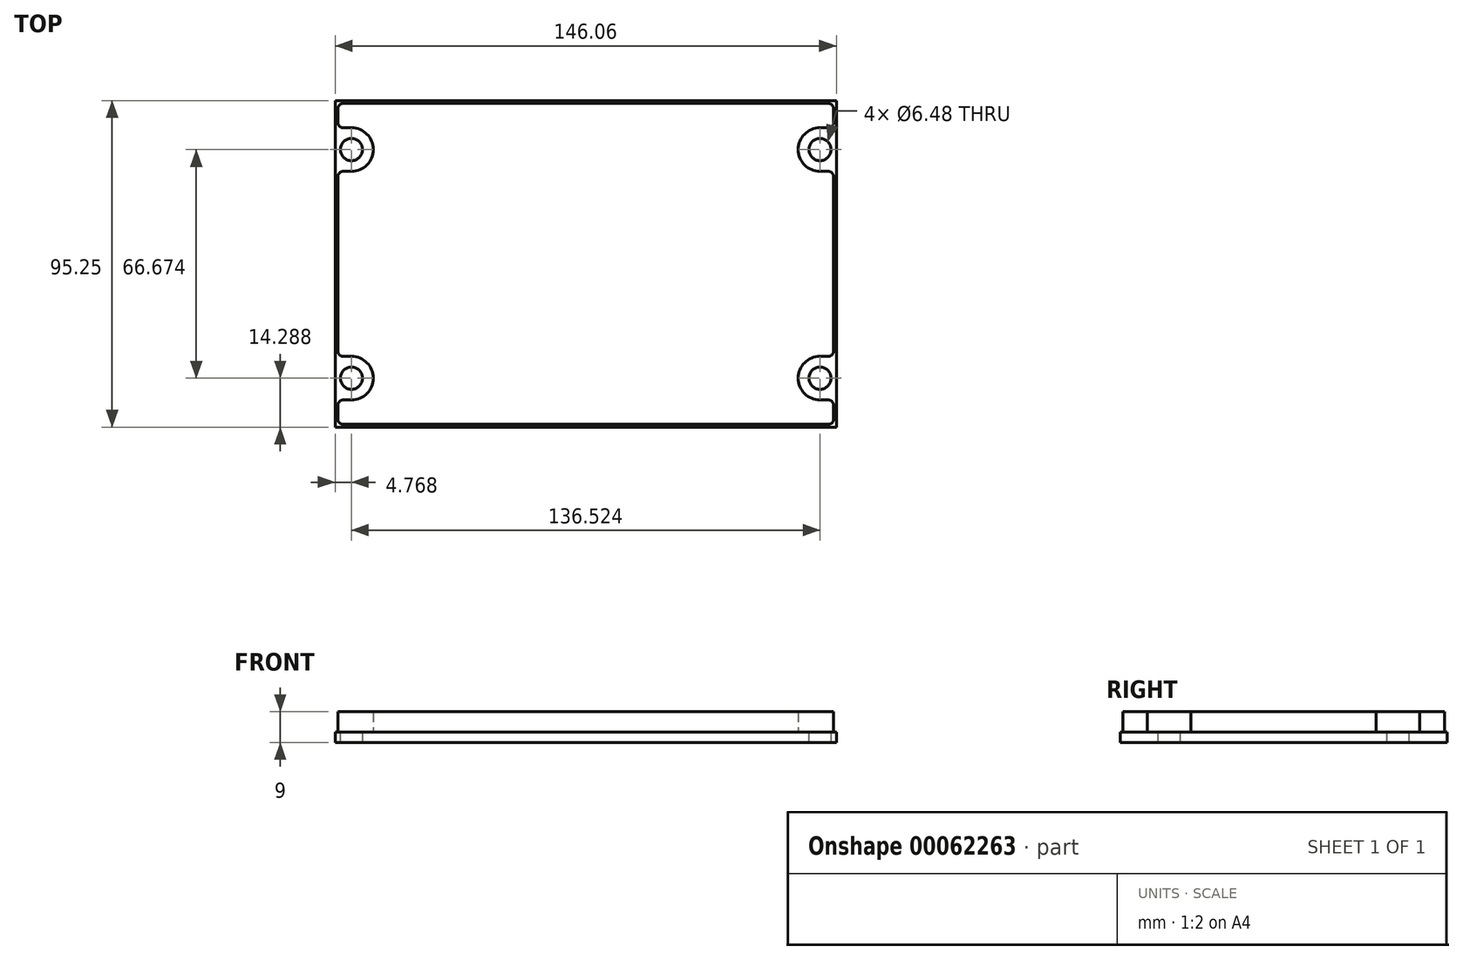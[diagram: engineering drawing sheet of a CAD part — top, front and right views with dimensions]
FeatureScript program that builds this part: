
annotation { "Feature Type Name" : "Feature", "Feature Type Description" : "" }
export const myFeature = defineFeature(function(context is Context, id is Id, definition is map)
    precondition{}
    {
        {
            var Q0;
            Q0=qCreatedBy(makeId("Top.planeOp"),FACE);
            var sketch = newSketch(context, id + "F0", { "sketchPlane" : qUnion([Q0])});
            skLineSegment(sketch, "E0.bottom", {"start": v(-73.03, 57.15) * mm, "end": v(73.03, 57.15) * mm});
            skLineSegment(sketch, "E0.top", {"start": v(-73.03, -38.1) * mm, "end": v(73.03, -38.1) * mm});
            skLineSegment(sketch, "E0.left", {"start": v(-73.03, 57.15) * mm, "end": v(-73.02, -38.1) * mm});
            skLineSegment(sketch, "E0.right", {"start": v(73.03, 57.15) * mm, "end": v(73.03, -38.1) * mm});
            skCircle(sketch, "E1", {"center": v(-68.26, 42.86) * mm, "radius": 3.24 * mm});
            skLineSegment(sketch, "E2", {"start": v(-73.03, 9.52) * mm, "end": v(-67.9, 9.52) * mm});
            skLineSegment(sketch, "E3.MirrorCS", {"start": v(73.03, 57.15) * mm, "end": v(73.02, -38.1) * mm});
            skCircle(sketch, "E4.MirrorC", {"center": v(68.26, 42.86) * mm, "radius": 3.24 * mm});
            skLineSegment(sketch, "E5.bottom", {"start": v(-72.23, 56.35) * mm, "end": v(72.23, 56.35) * mm});
            skLineSegment(sketch, "E5.top", {"start": v(-72.23, -37.3) * mm, "end": v(72.23, -37.3) * mm});
            skLineSegment(sketch, "E5.left", {"start": v(-72.22, 56.35) * mm, "end": v(-72.22, 49.21) * mm});
            skLineSegment(sketch, "E5.right", {"start": v(72.22, 56.35) * mm, "end": v(72.22, 49.21) * mm});
            skPoint(sketch, "E5.middle", {"position": v(0, 9.52) * mm});
            skPoint(sketch, "E5.middle.positionSnap0", {"position": v(0, 57.15) * mm});
            skPoint(sketch, "E5.centerSnap0", {"position": v(0, 57.15) * mm});
            skLineSegment(sketch, "E6.trimOffspring", {"start": v(-72.22, 36.51) * mm, "end": v(-72.22, -17.46) * mm});
            skCircle(sketch, "E7.MirrorC", {"center": v(-68.26, -23.81) * mm, "radius": 3.24 * mm});
            skLineSegment(sketch, "E8.trimOffspring", {"start": v(-72.22, -30.16) * mm, "end": v(-72.22, -37.3) * mm});
            skLineSegment(sketch, "E9", {"start": v(0, 59.28) * mm, "end": v(0, 57.15) * mm});
            skLineSegment(sketch, "E10.trimOffspring", {"start": v(72.22, 36.51) * mm, "end": v(72.22, -17.46) * mm});
            skLineSegment(sketch, "E11.trimOffspring", {"start": v(72.22, -30.16) * mm, "end": v(72.22, -37.3) * mm});
            skCircle(sketch, "E12.MirrorC", {"center": v(68.26, -23.81) * mm, "radius": 3.24 * mm});
            skLineSegment(sketch, "E13", {"start": v(-68.26, 49.21) * mm, "end": v(-72.22, 49.21) * mm});
            skLineSegment(sketch, "E14", {"start": v(-68.26, 36.51) * mm, "end": v(-72.22, 36.51) * mm});
            skArc(sketch, "E15.trimOffspring", {"start": v(-68.26, 36.51) * mm, "mid": v(-61.91, 42.86) * mm, "end": v(-68.26, 49.21) * mm});
            skLineSegment(sketch, "E16.MirrorCS", {"start": v(68.26, 49.21) * mm, "end": v(72.22, 49.21) * mm});
            skArc(sketch, "E17.MirrorCS", {"start": v(68.26, 36.51) * mm, "mid": v(61.91, 42.86) * mm, "end": v(68.26, 49.21) * mm});
            skLineSegment(sketch, "E18.MirrorCS", {"start": v(68.26, 36.51) * mm, "end": v(72.22, 36.51) * mm});
            skLineSegment(sketch, "E19.MirrorCS", {"start": v(-68.26, -30.16) * mm, "end": v(-72.22, -30.16) * mm});
            skArc(sketch, "E20.MirrorCS", {"start": v(-68.26, -17.46) * mm, "mid": v(-61.91, -23.81) * mm, "end": v(-68.26, -30.16) * mm});
            skLineSegment(sketch, "E21.MirrorCS", {"start": v(-68.26, -17.46) * mm, "end": v(-72.22, -17.46) * mm});
            skLineSegment(sketch, "E22.MirrorCS", {"start": v(68.26, -30.16) * mm, "end": v(72.23, -30.16) * mm});
            skArc(sketch, "E23.MirrorCS", {"start": v(68.26, -17.46) * mm, "mid": v(61.91, -23.81) * mm, "end": v(68.26, -30.16) * mm});
            skLineSegment(sketch, "E24.MirrorCS", {"start": v(68.26, -17.46) * mm, "end": v(72.23, -17.46) * mm});
            skSolve(sketch);
        }
        {
            var Q0;
            {var subQ3=sQuery(id+"F0.wireOp",EDGE,"E0.bottom");Q0=makeQuery(id+"F0.imprint","IMPRINT",FACE,{"disambiguationData":[TD([[makeQuery(id+"F0.imprint","IMPRINT",EDGE,{"derivedFrom":subQ3}),-1.0]])]});}
            var Q1;
            Q1=makeQuery(id+"F0.imprint","IMPRINT",FACE,{"disambiguationData":[TD([[makeQuery(id+"F0.imprint","IMPRINT",EDGE,{"derivedFrom":sQuery(id+"F0.wireOp",EDGE,"0KsHYRzl-QeBp-Sicu-B30s-vmT9e8yUwkHf")}),-1.0]])]});
            var Q2;
            {var subQ5=sQuery(id+"F0.wireOp",EDGE,"E0.top");Q2=makeQuery(id+"F0.imprint","IMPRINT",FACE,{"disambiguationData":[TD([[makeQuery(id+"F0.imprint","IMPRINT",EDGE,{"derivedFrom":subQ5}),1.0]])]});}
            var Q3;
            Q3=makeQuery(id+"F0.imprint","IMPRINT",FACE,{"disambiguationData":[TD([[makeQuery(id+"F0.imprint","IMPRINT",EDGE,{"derivedFrom":sQuery(id+"F0.wireOp",EDGE,"E5.bottom")}),-1.0]])]});
            extrude(context, id + "F1", {"entities" : qUnion([Q0, Q1, Q2, Q3]), "oppositeDirection" : true, "depth" : 3 * mm, "offsetDistance" : 25 * mm});
        }
        {
            var Q0;
            Q0=makeQuery(id+"F0.imprint","IMPRINT",FACE,{"disambiguationData":[TD([[makeQuery(id+"F0.imprint","IMPRINT",EDGE,{"derivedFrom":sQuery(id+"F0.wireOp",EDGE,"E5.bottom")}),-1.0]])]});
            extrude(context, id + "F2", {"entities" : qUnion([Q0]), "depth" : 6 * mm, "offsetDistance" : 25 * mm});
        }
        {
            var Q0;
            Q0=makeQuery(id+"F2.opExtrude","SWEPT_EDGE",EDGE,{"disambiguationData":[OSD([sQuery(id+"F0.wireOp",EDGE,"E5.bottom"),sQuery(id+"F0.wireOp",EDGE,"E5.left")])]});
            var Q1;
            Q1=makeQuery(id+"F2.opExtrude","SWEPT_EDGE",EDGE,{"disambiguationData":[OSD([sQuery(id+"F0.wireOp",EDGE,"E5.left"),sQuery(id+"F0.wireOp",EDGE,"KYFBzgIQ-4Zqs-6R5z-qhiH-rvfPci5RRXDs")])]});
            var Q2;
            Q2=makeQuery(id+"F2.opExtrude","SWEPT_EDGE",EDGE,{"disambiguationData":[OSD([sQuery(id+"F0.wireOp",EDGE,"y0Ednotj-fgLE-47Of-3iWq-vnumbfe9Me7E"),sQuery(id+"F0.wireOp",EDGE,"E6.trimOffspring")])]});
            var Q3;
            Q3=makeQuery(id+"F2.opExtrude","SWEPT_EDGE",EDGE,{"disambiguationData":[OSD([sQuery(id+"F0.wireOp",EDGE,"E6.trimOffspring"),sQuery(id+"F0.wireOp",EDGE,"553364b0-0c50-41da-a4d1-f82c899684470.MirrorCS")])]});
            var Q4;
            Q4=makeQuery(id+"F2.opExtrude","SWEPT_EDGE",EDGE,{"disambiguationData":[OSD([sQuery(id+"F0.wireOp",EDGE,"2d0b2af7-1972-4472-80e1-425fef26b84a0.MirrorCS"),sQuery(id+"F0.wireOp",EDGE,"E8.trimOffspring")])]});
            var Q5;
            Q5=makeQuery(id+"F2.opExtrude","SWEPT_EDGE",EDGE,{"disambiguationData":[OSD([sQuery(id+"F0.wireOp",EDGE,"E5.top"),sQuery(id+"F0.wireOp",EDGE,"E8.trimOffspring")])]});
            var Q6;
            Q6=makeQuery(id+"F2.opExtrude","SWEPT_EDGE",EDGE,{"disambiguationData":[OSD([sQuery(id+"F0.wireOp",EDGE,"E5.top"),sQuery(id+"F0.wireOp",EDGE,"E11.trimOffspring")])]});
            var Q7;
            Q7=makeQuery(id+"F2.opExtrude","SWEPT_EDGE",EDGE,{"disambiguationData":[OSD([sQuery(id+"F0.wireOp",EDGE,"6b0da2aa-3882-46fa-a501-ba939454f24d0.MirrorCS"),sQuery(id+"F0.wireOp",EDGE,"E11.trimOffspring")])]});
            var Q8;
            Q8=makeQuery(id+"F2.opExtrude","SWEPT_EDGE",EDGE,{"disambiguationData":[OSD([sQuery(id+"F0.wireOp",EDGE,"23beaa88-9077-45f1-bc4f-ba4309250fa40.MirrorCS"),sQuery(id+"F0.wireOp",EDGE,"E10.trimOffspring")])]});
            var Q9;
            Q9=makeQuery(id+"F2.opExtrude","SWEPT_EDGE",EDGE,{"disambiguationData":[OSD([sQuery(id+"F0.wireOp",EDGE,"E5.right"),sQuery(id+"F0.wireOp",EDGE,"76e7f314-1e51-4c87-a9a9-bf629407e17e0.MirrorCS")])]});
            var Q10;
            Q10=makeQuery(id+"F2.opExtrude","SWEPT_EDGE",EDGE,{"disambiguationData":[OSD([sQuery(id+"F0.wireOp",EDGE,"E5.bottom"),sQuery(id+"F0.wireOp",EDGE,"E5.right")])]});
            var Q11;
            Q11=makeQuery(id+"F2.opExtrude","SWEPT_EDGE",EDGE,{"disambiguationData":[OSD([sQuery(id+"F0.wireOp",EDGE,"fdf2bb90-056c-49c9-a4f4-28e15fb56c020.MirrorCS"),sQuery(id+"F0.wireOp",EDGE,"E10.trimOffspring")])]});
            fillet(context, id + "F3", {"entities" : qUnion([Q0, Q1, Q2, Q3, Q4, Q5, Q6, Q7, Q8, Q9, Q10, Q11]), "radius" : 1.59 * mm, "tangentPropagation" : true, "allowEdgeOverflow" : false});
        }
    });
